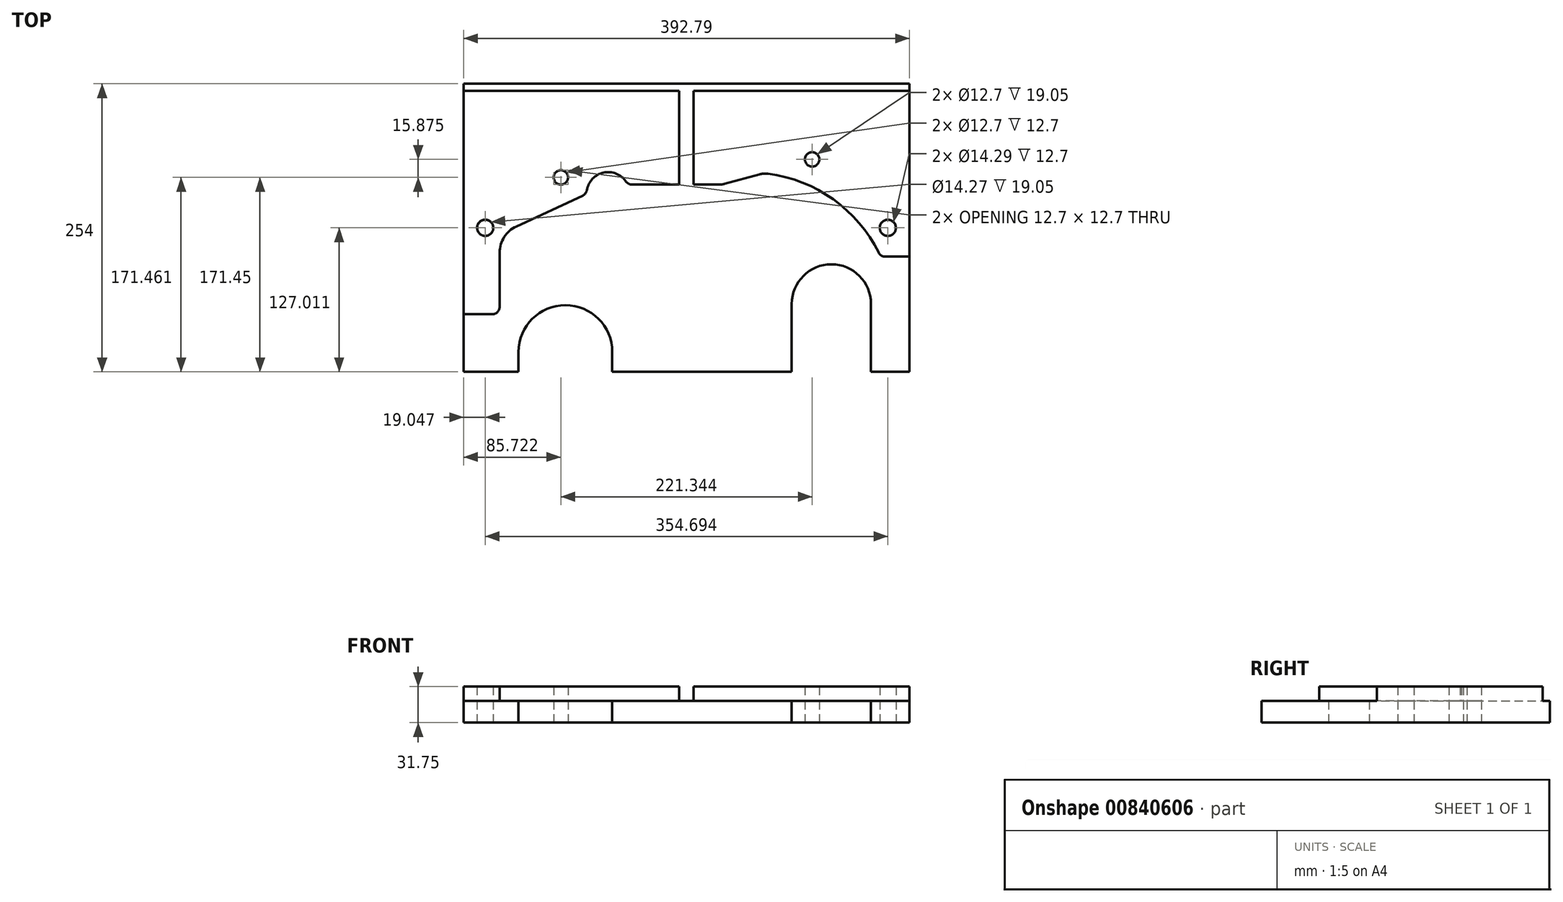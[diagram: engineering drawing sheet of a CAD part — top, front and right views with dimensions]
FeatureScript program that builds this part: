
annotation { "Feature Type Name" : "Feature", "Feature Type Description" : "" }
export const myFeature = defineFeature(function(context is Context, id is Id, definition is map)
    precondition{}
    {
        {
            var Q0;
            Q0=qCreatedBy(makeId("Top.planeOp"),FACE);
            var sketch = newSketch(context, id + "F0", { "sketchPlane" : qUnion([Q0])});
            skLineSegment(sketch, "E0", {"start": v(153.35, -127) * mm, "end": v(-112.4, -127) * mm});
            skArc(sketch, "E1", {"start": v(-112.4, -127) * mm, "mid": v(-149.75, -68.16) * mm, "end": v(-187.1, -127) * mm});
            skLineSegment(sketch, "E2", {"start": v(-187.1, -127) * mm, "end": v(-239.44, -127) * mm});
            skLineSegment(sketch, "E3", {"start": v(-239.44, -127) * mm, "end": v(-239.44, 127) * mm});
            skLineSegment(sketch, "E4", {"start": v(-239.44, 127) * mm, "end": v(153.35, 127) * mm});
            skLineSegment(sketch, "E5", {"start": v(153.35, 127) * mm, "end": v(153.35, -127) * mm});
            skCircle(sketch, "E6", {"center": v(-153.72, 44.45) * mm, "radius": 6.35 * mm});
            skCircle(sketch, "E7", {"center": v(67.63, 60.33) * mm, "radius": 6.35 * mm});
            skCircle(sketch, "E8", {"center": v(-220.4, 0) * mm, "radius": 7.14 * mm});
            skCircle(sketch, "E9", {"center": v(134.3, 0) * mm, "radius": 7.14 * mm});
            skCircle(sketch, "E10", {"center": v(84.58, -67.07) * mm, "radius": 34.93 * mm});
            skSolve(sketch);
        }
        {
            var Q0;
            Q0=qSketchRegion(id+"F0",true);
            extrude(context, id + "F1", {"entities" : qUnion([Q0]), "depth" : 19.05 * mm, "offsetDistance" : 25.4 * mm});
        }
        {
            var Q0;
            Q0=makeQuery(id+"F1.opExtrude","CAP_FACE",FACE,{"disambiguationData":[OSD([sQuery(id+"F0.wireOp",EDGE,"E0"),sQuery(id+"F0.wireOp",EDGE,"E1"),sQuery(id+"F0.wireOp",EDGE,"E2"),sQuery(id+"F0.wireOp",EDGE,"E3"),sQuery(id+"F0.wireOp",EDGE,"E4"),sQuery(id+"F0.wireOp",EDGE,"E5"),sQuery(id+"F0.wireOp",EDGE,"E8"),sQuery(id+"F0.wireOp",EDGE,"E10"),sQuery(id+"F0.wireOp",EDGE,"E9"),sQuery(id+"F0.wireOp",EDGE,"E6"),sQuery(id+"F0.wireOp",EDGE,"E7")])],"isStart":false});
            var sketch = newSketch(context, id + "F2", { "sketchPlane" : qUnion([Q0])});
            skArc(sketch, "E11", {"start": v(-193.03, 1.2) * mm, "mid": v(-203.71, -8.17) * mm, "end": v(-207.7, -21.82) * mm});
            skArc(sketch, "E12", {"start": v(28.82, 47.68) * mm, "mid": v(25.06, 47.8) * mm, "end": v(21.36, 47.17) * mm});
            skLineSegment(sketch, "E13", {"start": v(-9.42, 38.78) * mm, "end": v(21.36, 47.17) * mm});
            skArc(sketch, "E14", {"start": v(-14.43, 38.11) * mm, "mid": v(-11.9, 38.28) * mm, "end": v(-9.42, 38.78) * mm});
            skLineSegment(sketch, "E15", {"start": v(21.36, 47.17) * mm, "end": v(-9.42, 38.78) * mm});
            skArc(sketch, "E16", {"start": v(126.32, -21.97) * mm, "mid": v(86.3, 25.08) * mm, "end": v(28.82, 47.68) * mm});
            skCircle(sketch, "E17", {"center": v(-153.72, 44.46) * mm, "radius": 6.35 * mm});
            skCircle(sketch, "E18", {"center": v(67.63, 60.34) * mm, "radius": 6.35 * mm});
            skCircle(sketch, "E19", {"center": v(-220.4, 0.01) * mm, "radius": 7.14 * mm});
            skCircle(sketch, "E20", {"center": v(134.3, 0.01) * mm, "radius": 7.14 * mm});
            skLineSegment(sketch, "E21", {"start": v(-239.44, 120.66) * mm, "end": v(-49.4, 120.66) * mm});
            skLineSegment(sketch, "E22", {"start": v(-49.4, 120.66) * mm, "end": v(-239.44, 120.66) * mm});
            skLineSegment(sketch, "E23", {"start": v(-49.4, 120.66) * mm, "end": v(-49.4, 38.11) * mm});
            skLineSegment(sketch, "E24", {"start": v(-49.4, 38.11) * mm, "end": v(-49.4, 120.66) * mm});
            skLineSegment(sketch, "E25", {"start": v(-36.7, 38.11) * mm, "end": v(-36.7, 120.66) * mm});
            skLineSegment(sketch, "E26", {"start": v(-36.7, 120.66) * mm, "end": v(-36.7, 38.11) * mm});
            skLineSegment(sketch, "E27", {"start": v(-36.7, 120.66) * mm, "end": v(153.35, 120.66) * mm});
            skLineSegment(sketch, "E28", {"start": v(153.35, 120.66) * mm, "end": v(-36.7, 120.66) * mm});
            skLineSegment(sketch, "E29", {"start": v(-49.4, 38.11) * mm, "end": v(-91.17, 38.11) * mm});
            skLineSegment(sketch, "E30", {"start": v(-91.17, 38.11) * mm, "end": v(-49.4, 38.11) * mm});
            skLineSegment(sketch, "E31", {"start": v(-239.44, -76.19) * mm, "end": v(-239.44, 120.66) * mm});
            skLineSegment(sketch, "E32", {"start": v(-214.04, -76.19) * mm, "end": v(-239.44, -76.19) * mm});
            skArc(sketch, "E33", {"start": v(-214.04, -76.19) * mm, "mid": v(-209.55, -74.33) * mm, "end": v(-207.7, -69.84) * mm});
            skLineSegment(sketch, "E34", {"start": v(-207.7, -21.82) * mm, "end": v(-207.7, -69.84) * mm});
            skArc(sketch, "E35", {"start": v(-193.03, 1.2) * mm, "mid": v(-203.72, -8.17) * mm, "end": v(-207.7, -21.82) * mm});
            skLineSegment(sketch, "E36", {"start": v(-134.46, 28.51) * mm, "end": v(-193.03, 1.2) * mm});
            skArc(sketch, "E37", {"start": v(-134.46, 28.51) * mm, "mid": v(-132.09, 30.42) * mm, "end": v(-130.88, 33.22) * mm});
            skArc(sketch, "E38", {"start": v(-96.4, 40.86) * mm, "mid": v(-116.21, 48.66) * mm, "end": v(-130.88, 33.22) * mm});
            skArc(sketch, "E39", {"start": v(-96.4, 40.86) * mm, "mid": v(-94.12, 38.84) * mm, "end": v(-91.17, 38.11) * mm});
            skLineSegment(sketch, "E40", {"start": v(-239.44, -76.19) * mm, "end": v(-214.04, -76.19) * mm});
            skLineSegment(sketch, "E41", {"start": v(131.96, -25.39) * mm, "end": v(153.35, -25.39) * mm});
            skArc(sketch, "E42", {"start": v(126.27, -21.86) * mm, "mid": v(128.6, -24.44) * mm, "end": v(131.96, -25.39) * mm});
            skArc(sketch, "E43", {"start": v(126.27, -21.86) * mm, "mid": v(86.25, 25.12) * mm, "end": v(28.82, 47.68) * mm});
            skLineSegment(sketch, "E44", {"start": v(-36.7, 38.11) * mm, "end": v(-14.43, 38.11) * mm});
            skLineSegment(sketch, "E45", {"start": v(-193.03, 1.2) * mm, "end": v(-134.46, 28.51) * mm});
            skLineSegment(sketch, "E46", {"start": v(-207.7, -69.84) * mm, "end": v(-207.7, -21.82) * mm});
            skLineSegment(sketch, "E47", {"start": v(-239.44, 120.66) * mm, "end": v(-239.44, -76.19) * mm});
            skLineSegment(sketch, "E48", {"start": v(153.35, -25.39) * mm, "end": v(153.35, 120.66) * mm});
            skLineSegment(sketch, "E49", {"start": v(-14.43, 38.11) * mm, "end": v(-36.7, 38.11) * mm});
            skLineSegment(sketch, "E50", {"start": v(153.35, -25.39) * mm, "end": v(131.96, -25.39) * mm});
            skLineSegment(sketch, "E51", {"start": v(153.35, 120.66) * mm, "end": v(153.35, -25.39) * mm});
            skSolve(sketch);
        }
        {
            var Q0;
            Q0=qSketchRegion(id+"F2",true);
            extrude(context, id + "F3", {"entities" : qUnion([Q0]), "operationType" : NewBodyOperationType.ADD, "depth" : 12.7 * mm, "offsetDistance" : 25.4 * mm});
        }
        {
            var Q0;
            {var subQ0=sQuery(id+"F0.wireOp",EDGE,"E2");var subQ1=sQuery(id+"F0.wireOp",EDGE,"E1");var subQ2=sQuery(id+"F0.wireOp",EDGE,"E3");var subQ3=sQuery(id+"F0.wireOp",EDGE,"E0");var subQ4=sQuery(id+"F0.wireOp",EDGE,"E4");var subQ5=sQuery(id+"F0.wireOp",EDGE,"E5");var subQ6=sQuery(id+"F0.wireOp",EDGE,"E10");Q0=makeQuery(id+"F3.boolean.opBoolean","SPLIT",FACE,{"disambiguationData":[TD([makeQuery(id+"F1.opExtrude","SWEPT_FACE",FACE,{"disambiguationData":[OSD([subQ3])]})])],"derivedFrom":makeQuery(id+"F1.opExtrude","CAP_FACE",FACE,{"disambiguationData":[OSD([subQ3,subQ1,subQ0,subQ2,subQ4,subQ5,sQuery(id+"F0.wireOp",EDGE,"E8"),subQ6,sQuery(id+"F0.wireOp",EDGE,"E9"),sQuery(id+"F0.wireOp",EDGE,"E6"),sQuery(id+"F0.wireOp",EDGE,"E7")])],"isStart":false})});}
            var sketch = newSketch(context, id + "F4", { "sketchPlane" : qUnion([Q0])});
            skCircle(sketch, "E52", {"center": v(84.58, -67.07) * mm, "radius": 34.93 * mm});
            skLineSegment(sketch, "E53", {"start": v(119.5, -127) * mm, "end": v(119.5, -67.07) * mm});
            skLineSegment(sketch, "E54", {"start": v(49.65, -127) * mm, "end": v(49.65, -67.07) * mm});
            skLineSegment(sketch, "E55", {"start": v(49.65, -127) * mm, "end": v(119.5, -127) * mm});
            skSolve(sketch);
        }
        {
            var Q0;
            Q0=qSketchRegion(id+"F4",true);
            extrude(context, id + "F5", {"entities" : qUnion([Q0]), "operationType" : NewBodyOperationType.REMOVE, "oppositeDirection" : true, "depth" : 25.4 * mm, "offsetDistance" : 25.4 * mm});
        }
        {
            var Q0;
            {var subQ0=sQuery(id+"F0.wireOp",EDGE,"E2");var subQ1=sQuery(id+"F0.wireOp",EDGE,"E1");var subQ2=sQuery(id+"F0.wireOp",EDGE,"E3");var subQ3=sQuery(id+"F0.wireOp",EDGE,"E0");var subQ4=sQuery(id+"F0.wireOp",EDGE,"E4");var subQ5=sQuery(id+"F0.wireOp",EDGE,"E5");var subQ6=sQuery(id+"F0.wireOp",EDGE,"E10");Q0=makeQuery(id+"F3.boolean.opBoolean","SPLIT",FACE,{"disambiguationData":[TD([makeQuery(id+"F1.opExtrude","SWEPT_FACE",FACE,{"disambiguationData":[OSD([subQ3])]})])],"derivedFrom":makeQuery(id+"F1.opExtrude","CAP_FACE",FACE,{"disambiguationData":[OSD([subQ3,subQ1,subQ0,subQ2,subQ4,subQ5,sQuery(id+"F0.wireOp",EDGE,"E8"),subQ6,sQuery(id+"F0.wireOp",EDGE,"E9"),sQuery(id+"F0.wireOp",EDGE,"E6"),sQuery(id+"F0.wireOp",EDGE,"E7")])],"isStart":false})});}
            var sketch = newSketch(context, id + "F6", { "sketchPlane" : qUnion([Q0])});
            skArc(sketch, "E56", {"start": v(-108.47, -109.44) * mm, "mid": v(-149.75, -68.16) * mm, "end": v(-191.02, -109.44) * mm});
            skLineSegment(sketch, "E57", {"start": v(-108.47, -127) * mm, "end": v(-108.47, -109.44) * mm});
            skLineSegment(sketch, "E58", {"start": v(-191.02, -127) * mm, "end": v(-191.02, -109.44) * mm});
            skLineSegment(sketch, "E59", {"start": v(-191.02, -127) * mm, "end": v(-108.47, -127) * mm});
            skSolve(sketch);
        }
        {
            var Q0;
            Q0=qSketchRegion(id+"F6",true);
            extrude(context, id + "F7", {"entities" : qUnion([Q0]), "operationType" : NewBodyOperationType.REMOVE, "oppositeDirection" : true, "depth" : 25.4 * mm, "offsetDistance" : 25.4 * mm});
        }
    });
